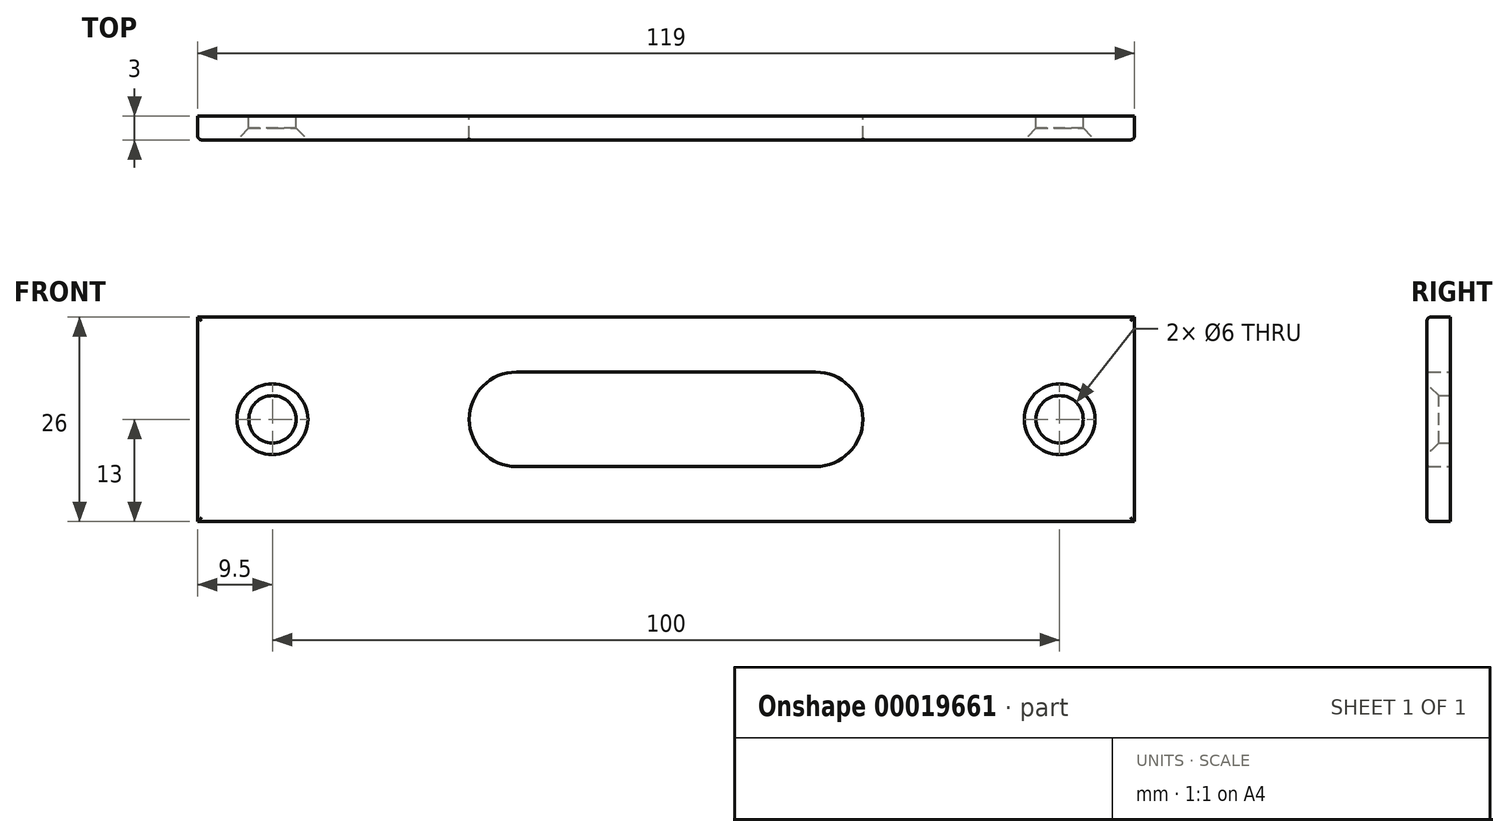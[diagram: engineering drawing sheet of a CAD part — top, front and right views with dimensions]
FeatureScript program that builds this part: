
annotation { "Feature Type Name" : "Feature", "Feature Type Description" : "" }
export const myFeature = defineFeature(function(context is Context, id is Id, definition is map)
    precondition{}
    {
        {
            var Q0;
            Q0=qCreatedBy(makeId("Front.planeOp"),FACE);
            var sketch = newSketch(context, id + "F0", { "sketchPlane" : qUnion([Q0])});
            skLineSegment(sketch, "E0.rect.bottom", {"start": v(59.5, -13) * mm, "end": v(-59.5, -13) * mm});
            skLineSegment(sketch, "E0.rect.top", {"start": v(59.5, 13) * mm, "end": v(-59.5, 13) * mm});
            skLineSegment(sketch, "E0.rect.left", {"start": v(59.5, -13) * mm, "end": v(59.5, 13) * mm});
            skLineSegment(sketch, "E0.rect.right", {"start": v(-59.5, -13) * mm, "end": v(-59.5, 13) * mm});
            skPoint(sketch, "E0.rect.middle", {"position": v(0, 0) * mm});
            skLineSegment(sketch, "E1.rect.bottom", {"start": v(-19, 6) * mm, "end": v(19, 6) * mm});
            skLineSegment(sketch, "E1.rect.top", {"start": v(-19, -6) * mm, "end": v(19, -6) * mm});
            skLineSegment(sketch, "E1.rect.left", {"start": v(-25, 0) * mm, "end": v(-25, 0) * mm});
            skLineSegment(sketch, "E1.rect.right", {"start": v(25, 0) * mm, "end": v(25, 0) * mm});
            skPoint(sketch, "E2.visualSharp", {"position": v(-25, 6) * mm});
            skArc(sketch, "E2.filletArc", {"start": v(-19, 6) * mm, "mid": v(-23.24, 4.24) * mm, "end": v(-25, 0) * mm});
            skPoint(sketch, "E3.visualSharp", {"position": v(25, 6) * mm});
            skArc(sketch, "E3.filletArc", {"start": v(25, 0) * mm, "mid": v(23.24, 4.24) * mm, "end": v(19, 6) * mm});
            skPoint(sketch, "E4.visualSharp", {"position": v(25, -6) * mm});
            skArc(sketch, "E4.filletArc", {"start": v(19, -6) * mm, "mid": v(23.24, -4.24) * mm, "end": v(25, 0) * mm});
            skPoint(sketch, "E5.visualSharp", {"position": v(-25, -6) * mm});
            skArc(sketch, "E5.filletArc", {"start": v(-25, 0) * mm, "mid": v(-23.24, -4.24) * mm, "end": v(-19, -6) * mm});
            skCircle(sketch, "E6", {"center": v(-50, 0) * mm, "radius": 3 * mm});
            skCircle(sketch, "E7", {"center": v(50, 0) * mm, "radius": 3 * mm});
            skSolve(sketch);
        }
        {
            var Q0;
            Q0=makeQuery(id+"F0.imprint","IMPRINT",FACE,{"disambiguationData":[TD([[makeQuery(id+"F0.imprint","IMPRINT",EDGE,{"derivedFrom":sQuery(id+"F0.wireOp",EDGE,"E0.rect.bottom")}),-1.0]])]});
            extrude(context, id + "F1", {"entities" : qUnion([Q0]), "depth" : 3 * mm});
        }
        {
            var Q0;
            Q0=makeQuery(id+"F1.opExtrude","CAP_EDGE",EDGE,{"disambiguationData":[OSD([sQuery(id+"F0.wireOp",EDGE,"E6")])],"isStart":false});
            chamfer(context, id + "F2", {"entities" : qUnion([Q0]), "width" : 1.5 * mm, "tangentPropagation" : true});
        }
        {
            var Q0;
            Q0=makeQuery(id+"F1.opExtrude","CAP_EDGE",EDGE,{"disambiguationData":[OSD([sQuery(id+"F0.wireOp",EDGE,"E7")])],"isStart":false});
            chamfer(context, id + "F3", {"entities" : qUnion([Q0]), "width" : 1.5 * mm, "tangentPropagation" : true});
        }
        {
            var Q0;
            Q0=makeQuery(id+"F1.opExtrude","CAP_EDGE",EDGE,{"disambiguationData":[OSD([sQuery(id+"F0.wireOp",EDGE,"E1.rect.bottom")])],"isStart":false});
            fillet(context, id + "F4", {"entities" : qUnion([Q0]), "radius" : .25 * mm, "tangentPropagation" : true, "allowEdgeOverflow" : false});
        }
        {
            var Q0;
            Q0=makeQuery(id+"F1.opExtrude","CAP_EDGE",EDGE,{"disambiguationData":[OSD([sQuery(id+"F0.wireOp",EDGE,"E0.rect.top")])],"isStart":false});
            var Q1;
            Q1=makeQuery(id+"F1.opExtrude","CAP_EDGE",EDGE,{"disambiguationData":[OSD([sQuery(id+"F0.wireOp",EDGE,"E0.rect.right")])],"isStart":false});
            var Q2;
            Q2=makeQuery(id+"F1.opExtrude","CAP_EDGE",EDGE,{"disambiguationData":[OSD([sQuery(id+"F0.wireOp",EDGE,"E0.rect.bottom")])],"isStart":false});
            var Q3;
            Q3=makeQuery(id+"F1.opExtrude","CAP_EDGE",EDGE,{"disambiguationData":[OSD([sQuery(id+"F0.wireOp",EDGE,"E0.rect.left")])],"isStart":false});
            fillet(context, id + "F5", {"entities" : qUnion([Q0, Q1, Q2, Q3]), "radius" : .5 * mm, "tangentPropagation" : true, "allowEdgeOverflow" : false});
        }
    });
